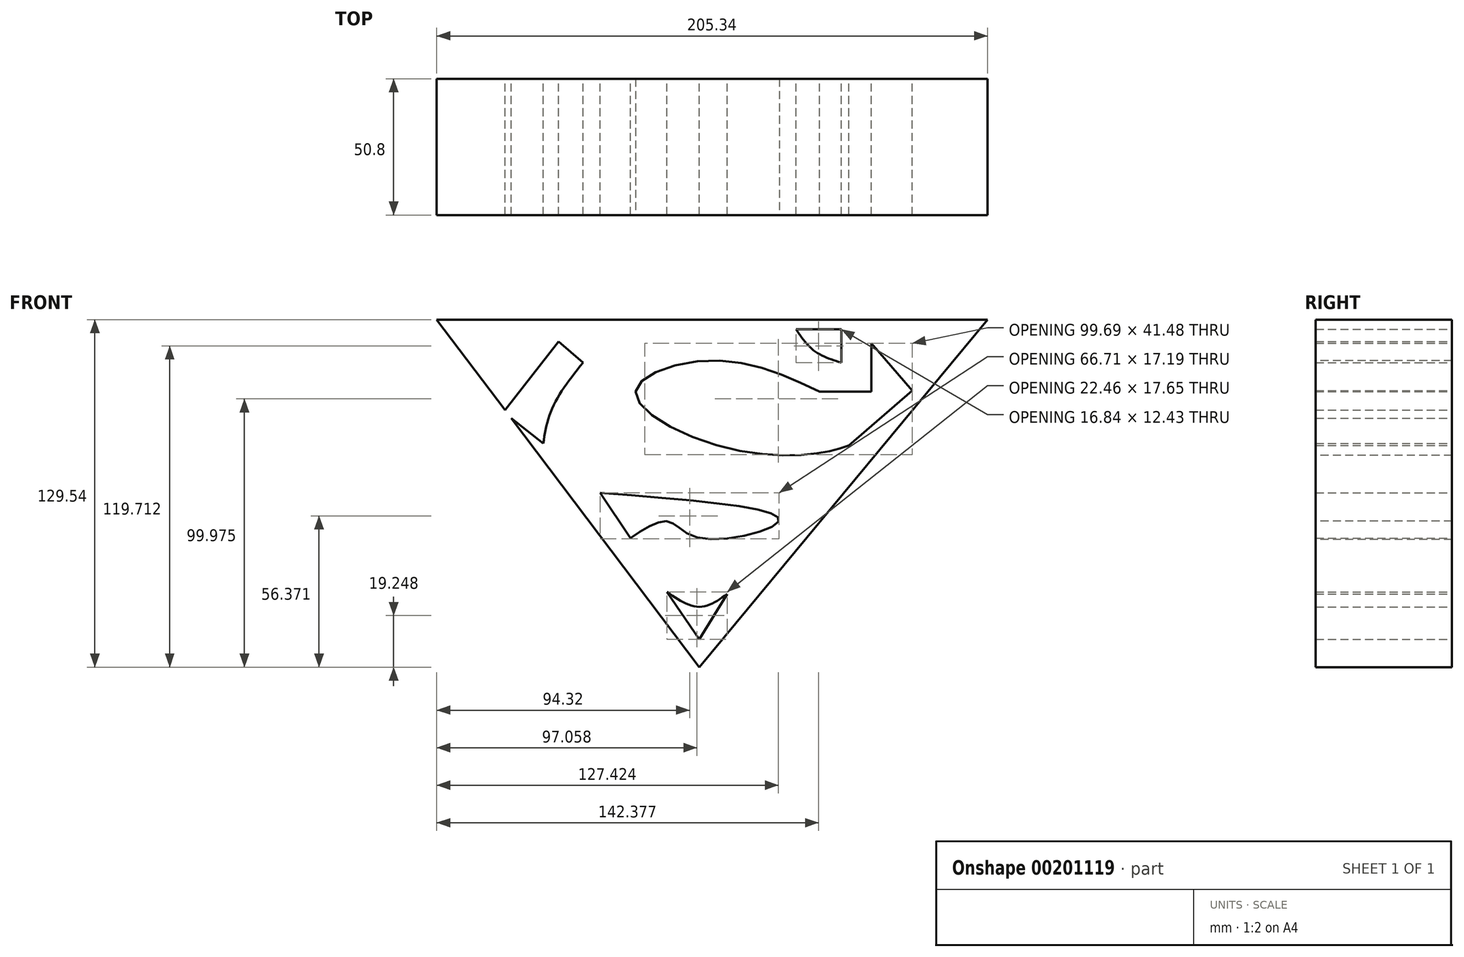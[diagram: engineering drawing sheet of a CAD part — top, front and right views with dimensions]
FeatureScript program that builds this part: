
annotation { "Feature Type Name" : "Feature", "Feature Type Description" : "" }
export const myFeature = defineFeature(function(context is Context, id is Id, definition is map)
    precondition{}
    {
        {
            var Q0;
            Q0=qCreatedBy(makeId("Front.planeOp"),FACE);
            var sketch = newSketch(context, id + "F0", { "sketchPlane" : qUnion([Q0])});
            skLineSegment(sketch, "E0", {"start": v(64.17, 66.37) * mm, "end": v(64.17, 48.33) * mm});
            skLineSegment(sketch, "E1", {"start": v(64.17, 48.33) * mm, "end": v(44.92, 48.33) * mm});
            skLineSegment(sketch, "E2", {"start": v(64.17, 66.37) * mm, "end": v(79.4, 48.73) * mm});
            skLineSegment(sketch, "E3", {"start": v(79.4, 48.73) * mm, "end": v(55.8, 28.34) * mm});
            skFitSpline(sketch, "E4", {"points": [v(44.92, 48.33) * mm, v(4.01, 59.96) * mm, v(-23.66, 48.33) * mm, v(6.82, 28.27) * mm, v(44.92, 25.47) * mm, v(55.8, 28.34) * mm], "startDerivative": vector(-163.28, 76.5) * mm, "endDerivative": vector(76.23, 26.32) * mm});
            skLineSegment(sketch, "E5", {"start": v(52.94, 71.59) * mm, "end": v(52.94, 59.16) * mm});
            skLineSegment(sketch, "E6", {"start": v(52.94, 59.16) * mm, "end": v(52.94, 71.59) * mm});
            skLineSegment(sketch, "E7", {"start": v(36.1, 71.59) * mm, "end": v(52.94, 71.59) * mm});
            skFitSpline(sketch, "E8", {"points": [v(52.94, 59.16) * mm, v(42.91, 63.57) * mm, v(36.1, 71.59) * mm], "startDerivative": vector(-21.4, 6.85) * mm, "endDerivative": vector(-12.27, 18.05) * mm});
            skFitSpline(sketch, "E9", {"points": [v(-58.15, 29.08) * mm, v(-54.54, 42.71) * mm, v(-43.31, 59.16) * mm], "startDerivative": vector(4.98, 29.73) * mm, "endDerivative": vector(24.15, 30.4) * mm});
            skLineSegment(sketch, "E10", {"start": v(-58.15, 29.08) * mm, "end": v(-73, 40.7) * mm});
            skLineSegment(sketch, "E11", {"start": v(-73, 40.7) * mm, "end": v(-52.4, 66.98) * mm});
            skLineSegment(sketch, "E12", {"start": v(-52.4, 66.98) * mm, "end": v(-43.31, 59.16) * mm});
            skLineSegment(sketch, "E13", {"start": v(-36.9, 10.63) * mm, "end": v(-25.67, -6.22) * mm});
            skFitSpline(sketch, "E14", {"points": [v(-25.67, -6.22) * mm, v(-11.63, 0) * mm, v(0, -6.22) * mm, v(29.68, 0) * mm, v(-36.9, 10.63) * mm], "startDerivative": vector(84.42, 56.37) * mm, "endDerivative": vector(-269.07, 20.84) * mm});
            skLineSegment(sketch, "E15", {"start": v(-12.03, -26.27) * mm, "end": v(0, -43.92) * mm});
            skLineSegment(sketch, "E16", {"start": v(0, -43.92) * mm, "end": v(10.43, -27.07) * mm});
            skFitSpline(sketch, "E17", {"points": [v(-12.03, -26.27) * mm, v(0, -31.88) * mm, v(10.43, -27.07) * mm], "startDerivative": vector(23.63, -16.23) * mm, "endDerivative": vector(21.26, 15) * mm});
            skLineSegment(sketch, "E18", {"start": v(0, -54.34) * mm, "end": v(107.48, 75.2) * mm});
            skLineSegment(sketch, "E19", {"start": v(107.48, 75.2) * mm, "end": v(-97.86, 75.2) * mm});
            skLineSegment(sketch, "E20", {"start": v(-97.86, 75.2) * mm, "end": v(0, -54.34) * mm});
            skSolve(sketch);
        }
        {
            var Q0;
            Q0=makeQuery(id+"F0.imprint","IMPRINT",FACE,{"disambiguationData":[TD([[makeQuery(id+"F0.imprint","IMPRINT",EDGE,{"derivedFrom":sQuery(id+"F0.wireOp",EDGE,"E0")}),-1.0]])]});
            extrude(context, id + "F1", {"entities" : qUnion([Q0]), "depth" : 25.4 * mm});
        }
        {
            var Q0;
            Q0=makeQuery(id+"F1.opExtrude","CAP_FACE",FACE,{"disambiguationData":[OSD([sQuery(id+"F0.wireOp",EDGE,"E0"),sQuery(id+"F0.wireOp",EDGE,"E1"),sQuery(id+"F0.wireOp",EDGE,"E2"),sQuery(id+"F0.wireOp",EDGE,"E3"),sQuery(id+"F0.wireOp",EDGE,"E4"),sQuery(id+"F0.wireOp",EDGE,"E6"),sQuery(id+"F0.wireOp",EDGE,"E7"),sQuery(id+"F0.wireOp",EDGE,"E8"),sQuery(id+"F0.wireOp",EDGE,"E9"),sQuery(id+"F0.wireOp",EDGE,"E10"),sQuery(id+"F0.wireOp",EDGE,"E11"),sQuery(id+"F0.wireOp",EDGE,"E12"),sQuery(id+"F0.wireOp",EDGE,"E13"),sQuery(id+"F0.wireOp",EDGE,"E14"),sQuery(id+"F0.wireOp",EDGE,"E15"),sQuery(id+"F0.wireOp",EDGE,"E16"),sQuery(id+"F0.wireOp",EDGE,"E17"),sQuery(id+"F0.wireOp",EDGE,"E18"),sQuery(id+"F0.wireOp",EDGE,"E19"),sQuery(id+"F0.wireOp",EDGE,"E20")])],"isStart":false});
            extrude(context, id + "F2", {"entities" : qUnion([Q0]), "operationType" : NewBodyOperationType.ADD, "depth" : 25.4 * mm});
        }
    });
